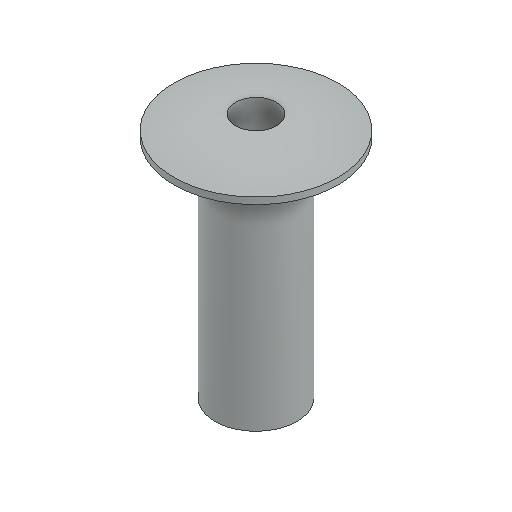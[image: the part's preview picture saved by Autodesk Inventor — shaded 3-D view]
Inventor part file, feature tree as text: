
AUTODESK INVENTOR PART (.ipt)
format: ipt  version: 2024.1 (Build 281209000, 209)  size: 114,688 bytes
history: native  units: in
note: dims shown in document units (in); Inventor stores cm internally (conversion verified against a paired STEP export)
features: revolve x1
ambient origin geometry x8: Origin, YZ Plane, XZ Plane, XY Plane, X Axis, Y Axis, Z Axis, Center Point
bodies: Solid1 (feature_tree)
feature tree (1):
  revolve  "Revolve1"  [1 undecoded]
note: 1 required parameter value undecoded (feature->parameter linkage not recoverable at this tier; creation-order binding heuristic only, values carry confidence <= 0.55)
